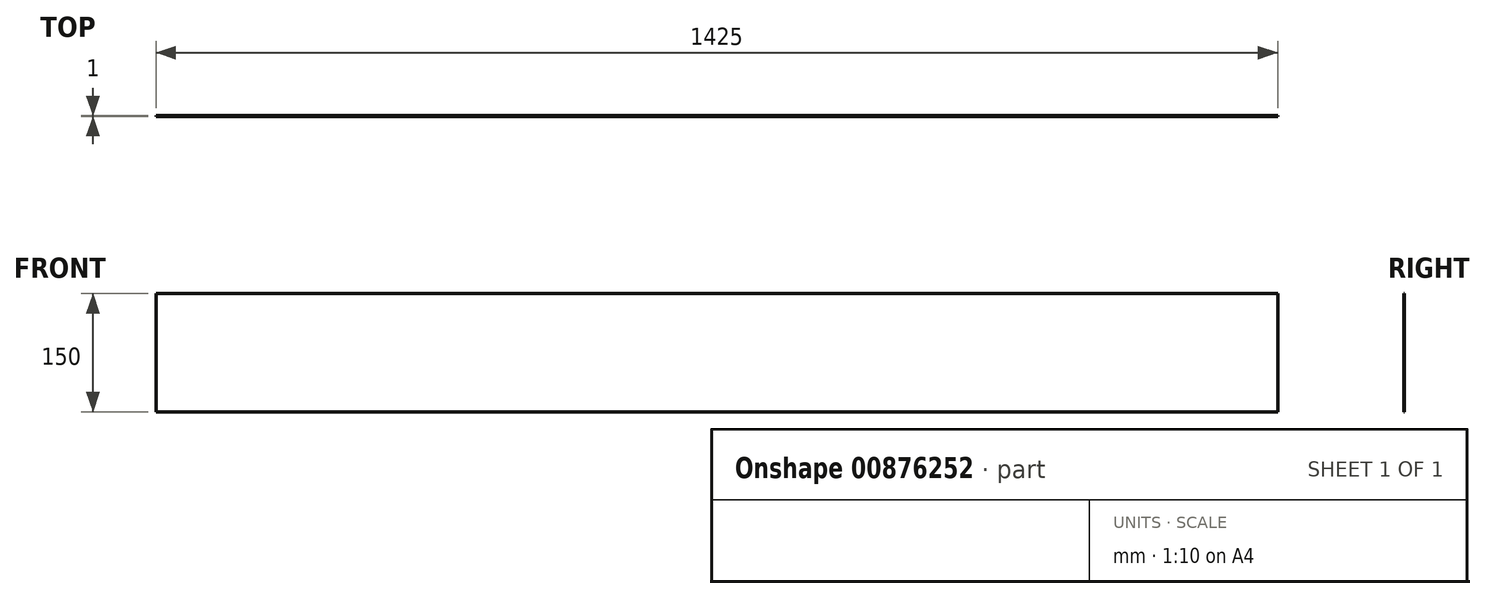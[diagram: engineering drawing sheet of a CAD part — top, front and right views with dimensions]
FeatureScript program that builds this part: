
annotation { "Feature Type Name" : "Feature", "Feature Type Description" : "" }
export const myFeature = defineFeature(function(context is Context, id is Id, definition is map)
    precondition{}
    {
        {
            var Q0;
            Q0=qCreatedBy(makeId("Front.planeOp"),FACE);
            var sketch = newSketch(context, id + "F0", { "sketchPlane" : qUnion([Q0])});
            skLineSegment(sketch, "E0.bottom", {"start": v(0, 0) * mm, "end": v(1425, 0) * mm});
            skLineSegment(sketch, "E0.top", {"start": v(0, -150) * mm, "end": v(1425, -150) * mm});
            skLineSegment(sketch, "E0.left", {"start": v(0, 0) * mm, "end": v(0, -150) * mm});
            skLineSegment(sketch, "E0.right", {"start": v(1425, 0) * mm, "end": v(1425, -150) * mm});
            skSolve(sketch);
        }
        {
            var Q0;
            Q0=makeQuery(id+"F0.imprint","IMPRINT",FACE,{"disambiguationData":[TD([[makeQuery(id+"F0.imprint","IMPRINT",EDGE,{"derivedFrom":sQuery(id+"F0.wireOp",EDGE,"E0.bottom")}),-1.0]])]});
            extrude(context, id + "F1", {"entities" : qUnion([Q0]), "depth" : 1 * mm, "offsetDistance" : 25.4 * mm});
        }
    });
